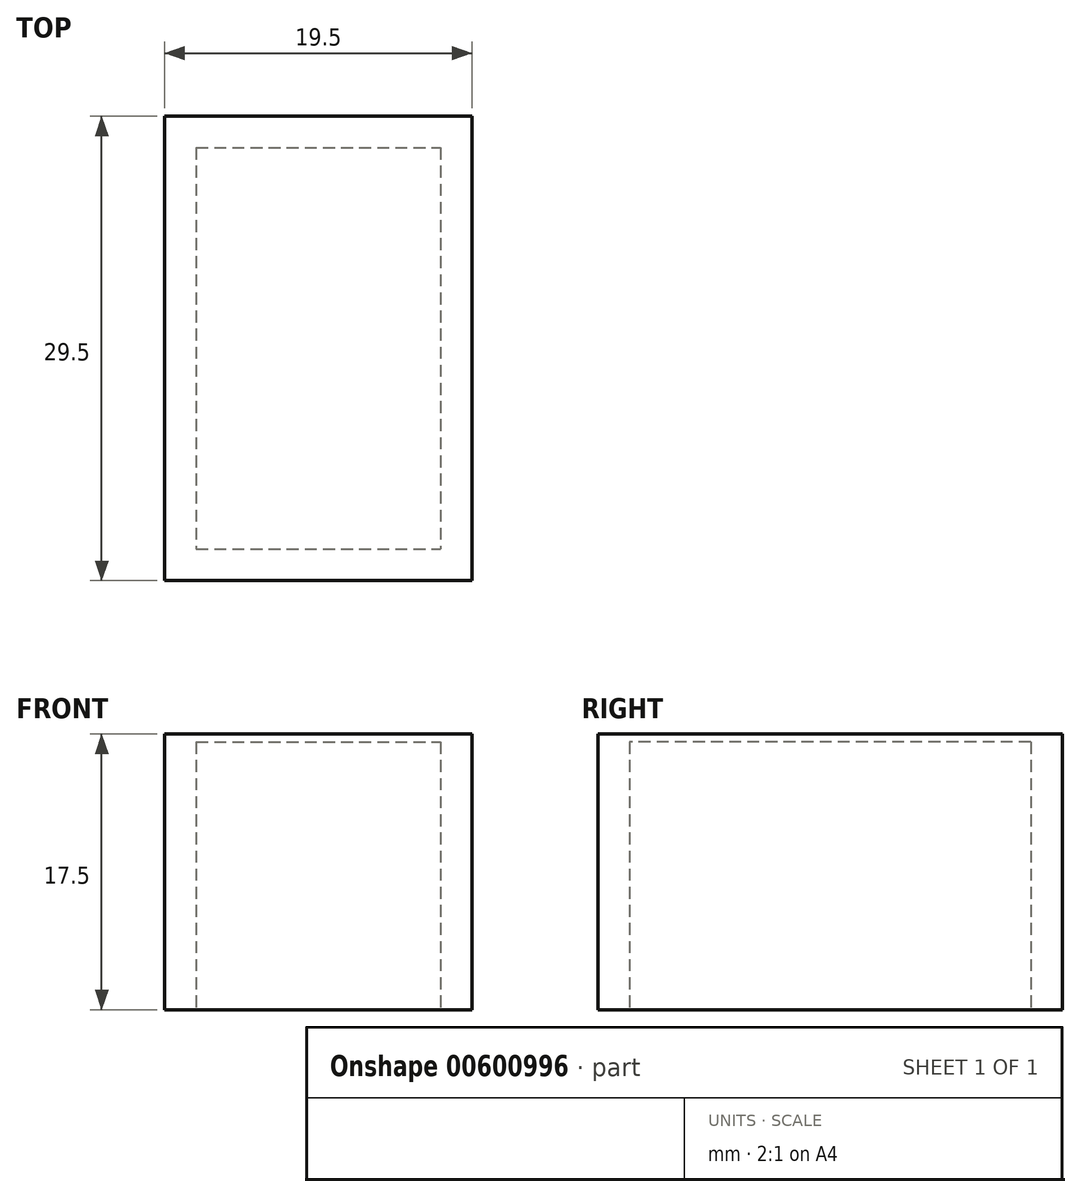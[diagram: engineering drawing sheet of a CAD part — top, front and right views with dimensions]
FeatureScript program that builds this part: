
annotation { "Feature Type Name" : "Feature", "Feature Type Description" : "" }
export const myFeature = defineFeature(function(context is Context, id is Id, definition is map)
    precondition{}
    {
        {
            var Q0;
            Q0=qCreatedBy(makeId("Top.planeOp"),FACE);
            var sketch = newSketch(context, id + "F0", { "sketchPlane" : qUnion([Q0])});
            skLineSegment(sketch, "E0.bottom", {"start": v(-9.75, 14.75) * mm, "end": v(9.75, 14.75) * mm});
            skLineSegment(sketch, "E0.top", {"start": v(-9.75, -14.75) * mm, "end": v(9.75, -14.75) * mm});
            skLineSegment(sketch, "E0.left", {"start": v(-9.75, 14.75) * mm, "end": v(-9.75, -14.75) * mm});
            skLineSegment(sketch, "E0.right", {"start": v(9.75, 14.75) * mm, "end": v(9.75, -14.75) * mm});
            skPoint(sketch, "E0.middle", {"position": v(0, 0) * mm});
            skSolve(sketch);
        }
        {
            var Q0;
            Q0=makeQuery(id+"F0.imprint","IMPRINT",FACE,{"disambiguationData":[TD([[makeQuery(id+"F0.imprint","IMPRINT",EDGE,{"derivedFrom":sQuery(id+"F0.wireOp",EDGE,"E0.bottom")}),-1.0]])]});
            extrude(context, id + "F1", {"entities" : qUnion([Q0]), "depth" : 17.5 * mm, "offsetDistance" : 25 * mm});
        }
        {
            var Q0;
            Q0=qCreatedBy(makeId("Top.planeOp"),FACE);
            var sketch = newSketch(context, id + "F2", { "sketchPlane" : qUnion([Q0])});
            skLineSegment(sketch, "E1.bottom", {"start": v(-7.75, 12.75) * mm, "end": v(7.75, 12.75) * mm});
            skLineSegment(sketch, "E1.top", {"start": v(-7.75, -12.75) * mm, "end": v(7.75, -12.75) * mm});
            skLineSegment(sketch, "E1.left", {"start": v(-7.75, 12.75) * mm, "end": v(-7.75, -12.75) * mm});
            skLineSegment(sketch, "E1.right", {"start": v(7.75, 12.75) * mm, "end": v(7.75, -12.75) * mm});
            skPoint(sketch, "E1.middle", {"position": v(0, 0) * mm});
            skSolve(sketch);
        }
        {
            var Q0;
            Q0=qSketchRegion(id+"F2",true);
            extrude(context, id + "F3", {"entities" : qUnion([Q0]), "operationType" : NewBodyOperationType.REMOVE, "depth" : 17 * mm, "offsetDistance" : 25 * mm});
        }
    });
